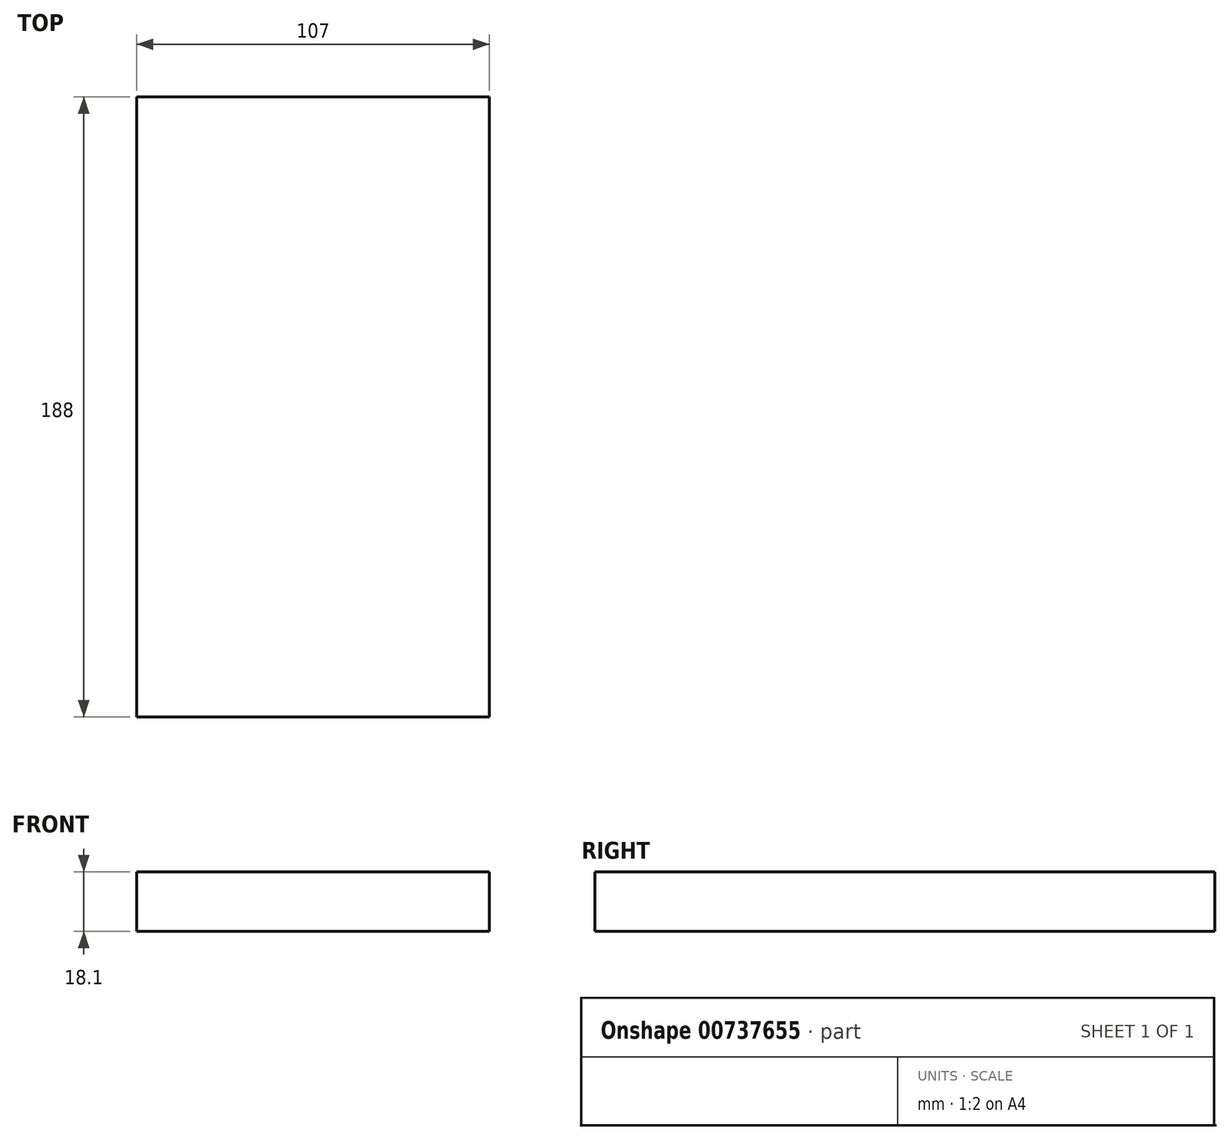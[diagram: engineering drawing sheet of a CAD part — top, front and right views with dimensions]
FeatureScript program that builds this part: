
annotation { "Feature Type Name" : "Feature", "Feature Type Description" : "" }
export const myFeature = defineFeature(function(context is Context, id is Id, definition is map)
    precondition{}
    {
        {
            var Q0;
            Q0=qCreatedBy(makeId("Top.planeOp"),FACE);
            var sketch = newSketch(context, id + "F0", { "sketchPlane" : qUnion([Q0])});
            skLineSegment(sketch, "E0.bottom", {"start": v(-53.5, 100) * mm, "end": v(53.5, 100) * mm});
            skLineSegment(sketch, "E0.top", {"start": v(-53.5, -100) * mm, "end": v(53.5, -100) * mm});
            skLineSegment(sketch, "E0.left", {"start": v(-53.5, 100) * mm, "end": v(-53.5, -100) * mm});
            skLineSegment(sketch, "E0.right", {"start": v(53.5, 100) * mm, "end": v(53.5, -100) * mm});
            skPoint(sketch, "E0.middle", {"position": v(0, 0) * mm});
            skSolve(sketch);
        }
        {
            var Q0;
            Q0=makeQuery(id+"F0.imprint","IMPRINT",FACE,{"disambiguationData":[TD([[makeQuery(id+"F0.imprint","IMPRINT",EDGE,{"derivedFrom":sQuery(id+"F0.wireOp",EDGE,"E0.bottom")}),-1.0]])]});
            extrude(context, id + "F1", {"entities" : qUnion([Q0]), "depth" : 18.1 * mm, "offsetDistance" : 25 * mm});
        }
        {
            var Q0;
            Q0=makeQuery(id+"F1.opExtrude","CAP_FACE",FACE,{"disambiguationData":[OSD([sQuery(id+"F0.wireOp",EDGE,"E0.bottom"),sQuery(id+"F0.wireOp",EDGE,"E0.top"),sQuery(id+"F0.wireOp",EDGE,"E0.left"),sQuery(id+"F0.wireOp",EDGE,"E0.right")])],"isStart":false});
            var sketch = newSketch(context, id + "F2", { "sketchPlane" : qUnion([Q0])});
            skLineSegment(sketch, "E1", {"start": v(-53.5, -88) * mm, "end": v(53.5, -88) * mm});
            skSolve(sketch);
        }
        {
            var Q0;
            {var subQ0=sQuery(id+"F2.wireOp",EDGE,"E1");Q0=makeQuery(id+"F2.imprint","IMPRINT",FACE,{"disambiguationData":[TD([[makeQuery(id+"F2.imprint","IMPRINT",EDGE,{"derivedFrom":subQ0}),-1.0]])]});}
            extrude(context, id + "F3", {"entities" : qUnion([Q0]), "operationType" : NewBodyOperationType.REMOVE, "oppositeDirection" : true, "depth" : 25 * mm, "offsetDistance" : 25 * mm});
        }
    });
